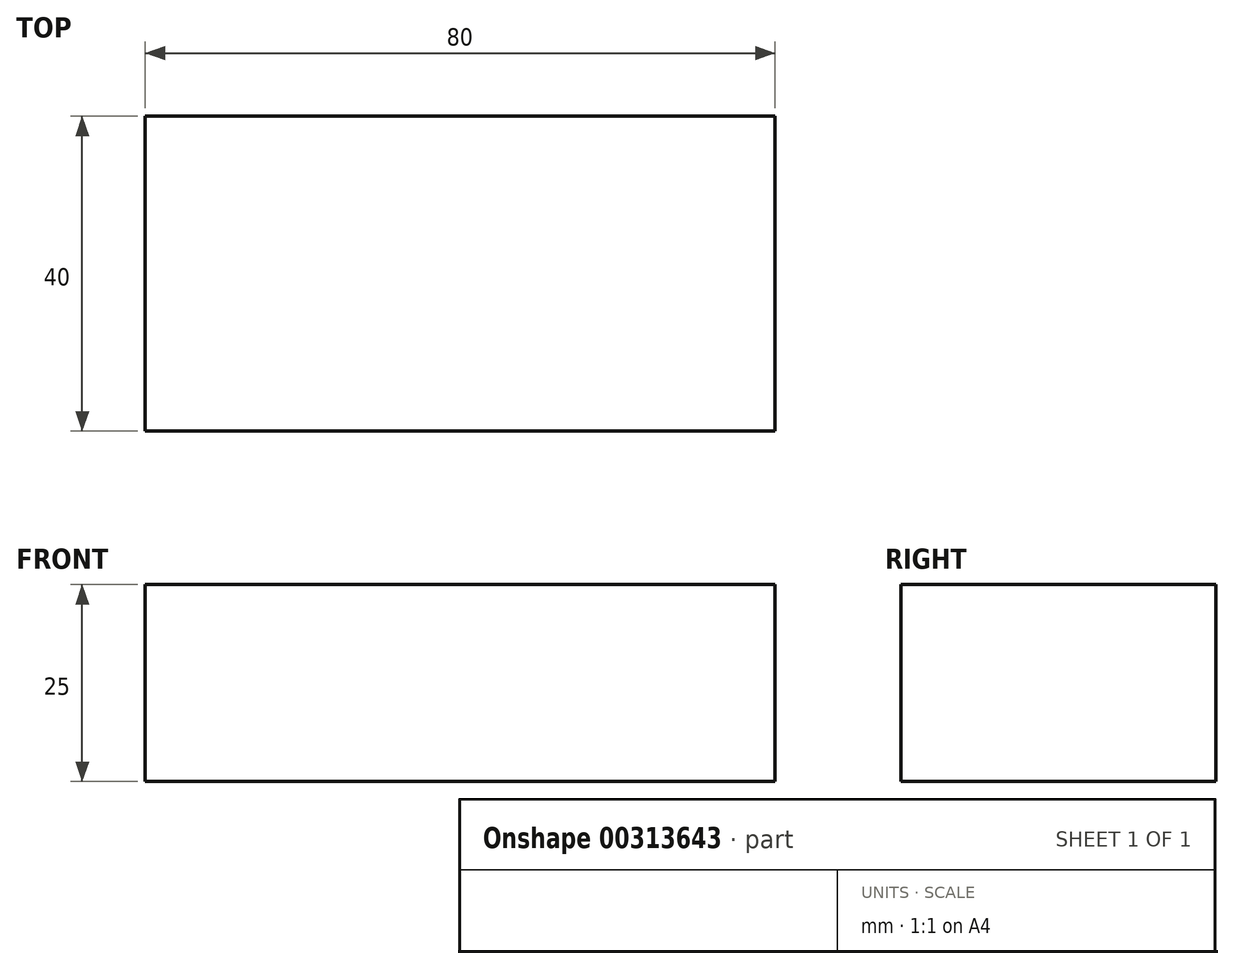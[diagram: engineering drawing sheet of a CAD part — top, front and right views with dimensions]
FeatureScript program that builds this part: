
annotation { "Feature Type Name" : "Feature", "Feature Type Description" : "" }
export const myFeature = defineFeature(function(context is Context, id is Id, definition is map)
    precondition{}
    {
        {
            var Q0;
            Q0=qCreatedBy(makeId("Top.planeOp"),FACE);
            var sketch = newSketch(context, id + "F0", { "sketchPlane" : qUnion([Q0])});
            skLineSegment(sketch, "E0.bottom", {"start": v(0, 0) * mm, "end": v(80, 0) * mm});
            skLineSegment(sketch, "E0.top", {"start": v(0, -40) * mm, "end": v(80, -40) * mm});
            skLineSegment(sketch, "E0.left", {"start": v(0, 0) * mm, "end": v(0, -40) * mm});
            skLineSegment(sketch, "E0.right", {"start": v(80, 0) * mm, "end": v(80, -40) * mm});
            skSolve(sketch);
        }
        {
            var Q0;
            Q0=makeQuery(id+"F0.imprint","IMPRINT",FACE,{"disambiguationData":[TD([[makeQuery(id+"F0.imprint","IMPRINT",EDGE,{"derivedFrom":sQuery(id+"F0.wireOp",EDGE,"E0.bottom")}),-1.0]])]});
            extrude(context, id + "F1", {"entities" : qUnion([Q0]), "depth" : 25 * mm});
        }
    });
